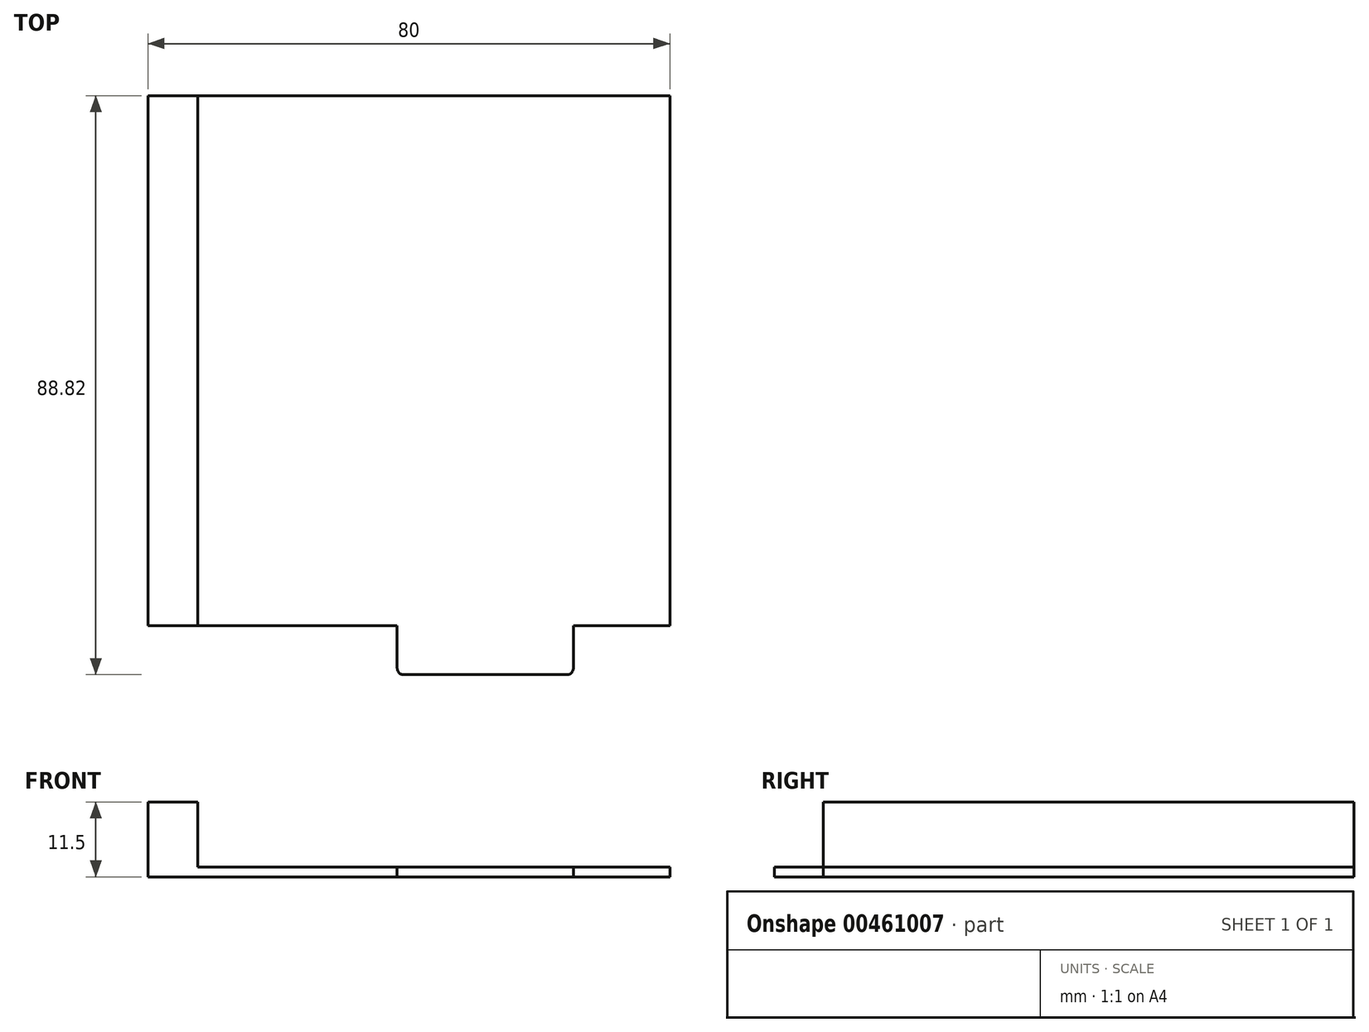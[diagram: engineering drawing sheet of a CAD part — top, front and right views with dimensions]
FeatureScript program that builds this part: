
annotation { "Feature Type Name" : "Feature", "Feature Type Description" : "" }
export const myFeature = defineFeature(function(context is Context, id is Id, definition is map)
    precondition{}
    {
        {
            var Q0;
            Q0=qCreatedBy(makeId("Top.planeOp"),FACE);
            var sketch = newSketch(context, id + "F0", { "sketchPlane" : qUnion([Q0])});
            skLineSegment(sketch, "E0.bottom", {"start": v(40, -40.66) * mm, "end": v(-40, -40.66) * mm});
            skLineSegment(sketch, "E0.top", {"start": v(40, 40.66) * mm, "end": v(-40, 40.66) * mm});
            skLineSegment(sketch, "E0.left", {"start": v(40, -40.66) * mm, "end": v(40, 40.66) * mm});
            skLineSegment(sketch, "E0.right", {"start": v(-40, -40.66) * mm, "end": v(-40, 40.66) * mm});
            skPoint(sketch, "E0.middle", {"position": v(0, 0) * mm});
            skSolve(sketch);
        }
        {
            var Q0;
            Q0 = qSketchRegion(id + "F0", true);
            extrude(context, id + "F1", {"entities" : qUnion([Q0]), "endBound" : BoundingType.SYMMETRIC, "depth" : 1.5 * mm});
        }
        {
            var Q0;
            Q0=makeQuery(id+"F1.opExtrude","CAP_FACE",FACE,{"disambiguationData":[OSD([sQuery(id+"F0.wireOp",EDGE,"E0.bottom"),sQuery(id+"F0.wireOp",EDGE,"E0.top"),sQuery(id+"F0.wireOp",EDGE,"E0.left"),sQuery(id+"F0.wireOp",EDGE,"E0.right")])],"isStart":false});
            var sketch = newSketch(context, id + "F2", { "sketchPlane" : qUnion([Q0])});
            skLineSegment(sketch, "E1", {"start": v(-1.8, -40.66) * mm, "end": v(25.2, -40.66) * mm});
            skSolve(sketch);
        }
        {
            var Q0;
            Q0=sQuery(id+"F2.wireOp",EDGE,"E1");
            extrude(context, id + "F3", {"bodyType" : ToolBodyType.SURFACE, "surfaceEntities" : qUnion([Q0]), "oppositeDirection" : true, "depth" : 1.5 * mm});
        }
        {
            var Q0;
            Q0=makeQuery(id+"F3.opExtrude","SWEPT_FACE",FACE,{"disambiguationData":[OSD([sQuery(id+"F2.wireOp",EDGE,"E1")])]});
            extrude(context, id + "F4", {"entities" : qUnion([Q0]), "operationType" : NewBodyOperationType.ADD, "oppositeDirection" : true, "depth" : 7.5 * mm});
        }
        {
            var Q0;
            Q0=makeQuery(id+"F4.opExtrude","CAP_EDGE",EDGE,{"disambiguationData":[OSD([sQuery(id+"F2.wireOp",VERTEX,"E1.start")])],"isStart":false});
            fillet(context, id + "F5", {"entities" : qUnion([Q0]), "radius" : 1 * mm, "tangentPropagation" : true, "allowEdgeOverflow" : false});
        }
        {
            var Q0;
            Q0=makeQuery(id+"F4.opExtrude","CAP_EDGE",EDGE,{"disambiguationData":[OSD([sQuery(id+"F2.wireOp",VERTEX,"E1.end")])],"isStart":false});
            fillet(context, id + "F6", {"entities" : qUnion([Q0]), "radius" : 1 * mm, "tangentPropagation" : true, "allowEdgeOverflow" : false});
        }
        {
            var Q0;
            {var subQ0=sQuery(id+"F2.wireOp",EDGE,"E1");Q0=makeQuery(id+"F4.boolean.opBoolean","MERGE",FACE,{"derivedFrom":[makeQuery(id+"F1.opExtrude","CAP_FACE",FACE,{"disambiguationData":[OSD([sQuery(id+"F0.wireOp",EDGE,"E0.bottom"),sQuery(id+"F0.wireOp",EDGE,"E0.top"),sQuery(id+"F0.wireOp",EDGE,"E0.left"),sQuery(id+"F0.wireOp",EDGE,"E0.right")])],"isStart":false}),makeQuery(id+"F4.opExtrude","SWEPT_FACE",FACE,{"disambiguationData":[OSD([subQ0]),TDD([makeQuery(id+"F3.opExtrude","CAP_EDGE",EDGE,{"disambiguationData":[OSD([subQ0])],"isStart":true})])]})]});}
            var sketch = newSketch(context, id + "F7", { "sketchPlane" : qUnion([Q0])});
            skLineSegment(sketch, "E2.bottom", {"start": v(-40, 40.66) * mm, "end": v(-32.4, 40.66) * mm});
            skLineSegment(sketch, "E2.top", {"start": v(-40, -40.66) * mm, "end": v(-32.4, -40.66) * mm});
            skLineSegment(sketch, "E2.left", {"start": v(-40, 40.66) * mm, "end": v(-40, -40.66) * mm});
            skLineSegment(sketch, "E2.right", {"start": v(-32.4, 40.66) * mm, "end": v(-32.4, -40.66) * mm});
            skSolve(sketch);
        }
        {
            var Q0;
            Q0 = qSketchRegion(id + "F7", true);
            extrude(context, id + "F8", {"entities" : qUnion([Q0]), "operationType" : NewBodyOperationType.ADD, "depth" : 10 * mm});
        }
    });
